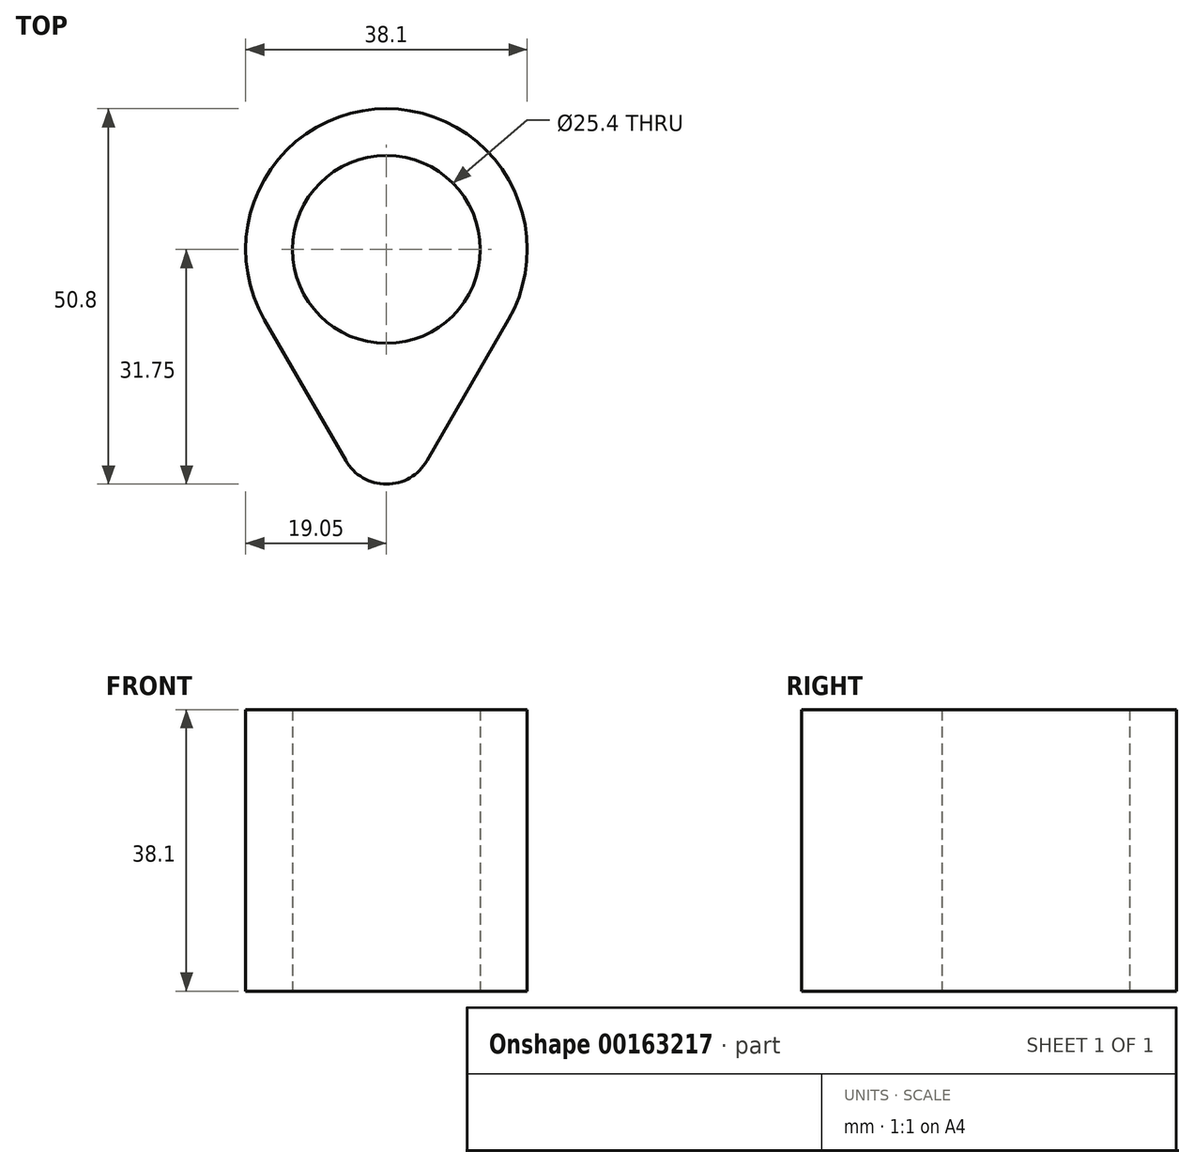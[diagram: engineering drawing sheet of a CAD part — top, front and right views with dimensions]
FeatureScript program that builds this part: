
annotation { "Feature Type Name" : "Feature", "Feature Type Description" : "" }
export const myFeature = defineFeature(function(context is Context, id is Id, definition is map)
    precondition{}
    {
        {
            var Q0;
            Q0=qCreatedBy(makeId("Top.planeOp"),FACE);
            var sketch = newSketch(context, id + "F0", { "sketchPlane" : qUnion([Q0])});
            skCircle(sketch, "E0", {"center": v(0, 0) * mm, "radius": 12.7 * mm});
            skArc(sketch, "E1", {"start": v(16.5, -9.53) * mm, "mid": v(0, 19.05) * mm, "end": v(-16.5, -9.52) * mm});
            skArc(sketch, "E2", {"start": v(-5.5, -28.58) * mm, "mid": v(0, -31.75) * mm, "end": v(5.5, -28.58) * mm});
            skLineSegment(sketch, "E3", {"start": v(-16.5, -9.52) * mm, "end": v(-5.5, -28.58) * mm});
            skLineSegment(sketch, "E4", {"start": v(16.5, -9.52) * mm, "end": v(5.5, -28.58) * mm});
            skSolve(sketch);
        }
        {
            var Q0;
            Q0=makeQuery(id+"F0.imprint","IMPRINT",FACE,{"disambiguationData":[TD([[makeQuery(id+"F0.imprint","IMPRINT",EDGE,{"derivedFrom":sQuery(id+"F0.wireOp",EDGE,"E0")}),-1.0]])]});
            extrude(context, id + "F1", {"entities" : qUnion([Q0]), "depth" : 38.1 * mm});
        }
    });
